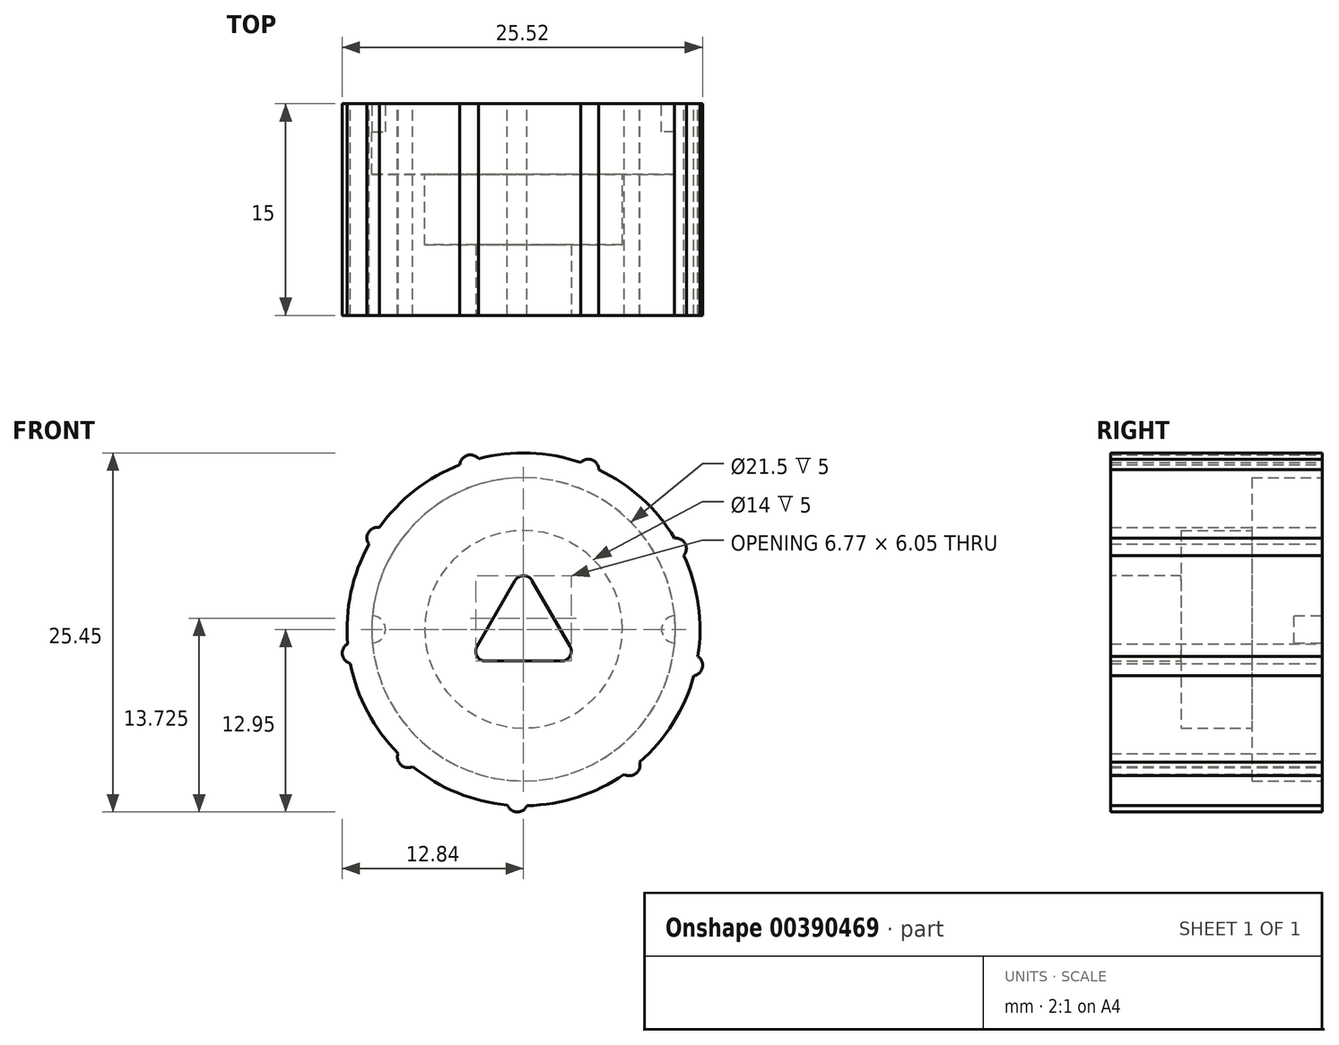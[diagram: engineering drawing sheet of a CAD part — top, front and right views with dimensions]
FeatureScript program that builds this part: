
annotation { "Feature Type Name" : "Feature", "Feature Type Description" : "" }
export const myFeature = defineFeature(function(context is Context, id is Id, definition is map)
    precondition{}
    {
        {
            var Q0;
            Q0=qCreatedBy(makeId("Front.planeOp"),FACE);
            var sketch = newSketch(context, id + "F0", { "sketchPlane" : qUnion([Q0])});
            skCircle(sketch, "E0", {"center": v(0, 0) * mm, "radius": 12.5 * mm});
            skCircle(sketch, "E1.cCircle", {"center": v(0, 0) * mm, "radius": 4.5 * mm, "construction": true});
            skLineSegment(sketch, "E1.0", {"start": v(0, 4.5) * mm, "end": v(3.9, -2.25) * mm});
            skLineSegment(sketch, "E1.1", {"start": v(3.9, -2.25) * mm, "end": v(-3.9, -2.25) * mm});
            skLineSegment(sketch, "E1.2", {"start": v(-3.9, -2.25) * mm, "end": v(0, 4.5) * mm});
            skSolve(sketch);
        }
        {
            var Q0;
            Q0=makeQuery(id+"F0.imprint","IMPRINT",FACE,{"disambiguationData":[TD([[makeQuery(id+"F0.imprint","IMPRINT",EDGE,{"derivedFrom":sQuery(id+"F0.wireOp",EDGE,"E0")}),1.0]])]});
            var Q1;
            Q1=sQuery(id+"F0.wireOp",EDGE,"E0");
            extrude(context, id + "F1", {"entities" : qUnion([Q0]), "surfaceEntities" : qUnion([Q1]), "depth" : 15 * mm});
        }
        {
            var Q0;
            Q0=makeQuery(id+"F1.opExtrude","CAP_FACE",FACE,{"disambiguationData":[OSD([sQuery(id+"F0.wireOp",EDGE,"E0"),sQuery(id+"F0.wireOp",EDGE,"E1.0"),sQuery(id+"F0.wireOp",EDGE,"E1.1"),sQuery(id+"F0.wireOp",EDGE,"E1.2")])],"isStart":true});
            var sketch = newSketch(context, id + "F2", { "sketchPlane" : qUnion([Q0])});
            skCircle(sketch, "E2", {"center": v(0, 0) * mm, "radius": 10.75 * mm});
            skSolve(sketch);
        }
        {
            var Q0;
            Q0=makeQuery(id+"F2.imprint","IMPRINT",FACE,{"disambiguationData":[TD([[makeQuery(id+"F2.imprint","IMPRINT",EDGE,{"derivedFrom":sQuery(id+"F2.wireOp",EDGE,"E2")}),1.0]])]});
            var Q1;
            Q1=sQuery(id+"F2.wireOp",EDGE,"E2");
            extrude(context, id + "F3", {"entities" : qUnion([Q0]), "operationType" : NewBodyOperationType.REMOVE, "surfaceEntities" : qUnion([Q1]), "oppositeDirection" : true, "depth" : 5 * mm});
        }
        {
            var Q0;
            Q0=makeQuery(id+"F3.boolean.opBoolean","COPY",FACE,{"derivedFrom":makeQuery(id+"F3.opExtrude","CAP_FACE",FACE,{"disambiguationData":[OSD([sQuery(id+"F0.wireOp",EDGE,"E1.0"),sQuery(id+"F0.wireOp",EDGE,"E1.1"),sQuery(id+"F0.wireOp",EDGE,"E1.2"),sQuery(id+"F2.wireOp",EDGE,"E2")])],"isStart":false})});
            var sketch = newSketch(context, id + "F4", { "sketchPlane" : qUnion([Q0])});
            skCircle(sketch, "E3", {"center": v(0, 0) * mm, "radius": 7 * mm});
            skSolve(sketch);
        }
        {
            var Q0;
            Q0 = qSketchRegion(id + "F4", true);
            extrude(context, id + "F5", {"entities" : qUnion([Q0]), "operationType" : NewBodyOperationType.REMOVE, "oppositeDirection" : true, "depth" : 5 * mm});
        }
        {
            var Q0;
            Q0=makeQuery(id+"F1.opExtrude","SWEPT_EDGE",EDGE,{"disambiguationData":[OSD([sQuery(id+"F0.wireOp",EDGE,"E1.0"),sQuery(id+"F0.wireOp",EDGE,"E1.2")])]});
            var Q1;
            Q1=makeQuery(id+"F1.opExtrude","SWEPT_EDGE",EDGE,{"disambiguationData":[OSD([sQuery(id+"F0.wireOp",EDGE,"E1.1"),sQuery(id+"F0.wireOp",EDGE,"E1.2")])]});
            var Q2;
            Q2=makeQuery(id+"F1.opExtrude","SWEPT_EDGE",EDGE,{"disambiguationData":[OSD([sQuery(id+"F0.wireOp",EDGE,"E1.0"),sQuery(id+"F0.wireOp",EDGE,"E1.1")])]});
            fillet(context, id + "F6", {"entities" : qUnion([Q0, Q1, Q2]), "radius" : 0.7 * mm, "tangentPropagation" : true, "allowEdgeOverflow" : false});
        }
        {
            var Q0;
            Q0=makeQuery(id+"F1.opExtrude","CAP_FACE",FACE,{"disambiguationData":[OSD([sQuery(id+"F0.wireOp",EDGE,"E0"),sQuery(id+"F0.wireOp",EDGE,"E1.0"),sQuery(id+"F0.wireOp",EDGE,"E1.1"),sQuery(id+"F0.wireOp",EDGE,"E1.2")])],"isStart":true});
            var sketch = newSketch(context, id + "F7", { "sketchPlane" : qUnion([Q0])});
            skCircle(sketch, "E4", {"center": v(-10.75, 0) * mm, "radius": 0.97 * mm});
            skCircle(sketch, "E5.1.0", {"center": v(10.75, 0) * mm, "radius": 0.97 * mm});
            skPoint(sketch, "E5.center", {"position": v(0, 0) * mm});
            skSolve(sketch);
        }
        {
            var Q0;
            {var subQ0=sQuery(id+"F7.wireOp",EDGE,"E4");var subQ1=makeQuery(id+"F3.boolean.opBoolean","COPY",EDGE,{"derivedFrom":makeQuery(id+"F3.opExtrude","CAP_EDGE",EDGE,{"disambiguationData":[OSD([sQuery(id+"F2.wireOp",EDGE,"E2")])],"isStart":true})});var subQ2=makeQuery(id+"F7.imprint","INTERSECT",VERTEX,{"disambiguationData":[OD(0.0)],"derivedFrom":[subQ1,subQ0]});Q0=makeQuery(id+"F7.imprint","IMPRINT",FACE,{"disambiguationData":[TD([[makeQuery(id+"F7.imprint","IMPRINT",EDGE,{"disambiguationData":[TD([[subQ2,-1.0]])],"derivedFrom":subQ0}),1.0]])]});}
            var Q1;
            {var subQ0=sQuery(id+"F7.wireOp",EDGE,"E5.1.0");var subQ1=makeQuery(id+"F3.boolean.opBoolean","COPY",EDGE,{"derivedFrom":makeQuery(id+"F3.opExtrude","CAP_EDGE",EDGE,{"disambiguationData":[OSD([sQuery(id+"F2.wireOp",EDGE,"E2")])],"isStart":true})});var subQ2=makeQuery(id+"F7.imprint","INTERSECT",VERTEX,{"disambiguationData":[OD(0.0)],"derivedFrom":[subQ1,subQ0]});Q1=makeQuery(id+"F7.imprint","IMPRINT",FACE,{"disambiguationData":[TD([[makeQuery(id+"F7.imprint","IMPRINT",EDGE,{"disambiguationData":[TD([[subQ2,1.0]])],"derivedFrom":subQ0}),1.0]])]});}
            extrude(context, id + "F8", {"entities" : qUnion([Q0, Q1]), "operationType" : NewBodyOperationType.ADD, "oppositeDirection" : true, "depth" : 2 * mm, "offsetDistance" : 25 * mm});
        }
        {
            var Q0;
            Q0=qCreatedBy(makeId("Front.planeOp"),FACE);
            var sketch = newSketch(context, id + "F9", { "sketchPlane" : qUnion([Q0])});
            skCircle(sketch, "E6", {"center": v(-10.34, 6.48) * mm, "radius": 0.75 * mm});
            skLineSegment(sketch, "E7", {"start": v(0, 14.1) * mm, "end": v(0, -18.46) * mm});
            skCircle(sketch, "E8.1.0", {"center": v(-12.09, -1.69) * mm, "radius": 0.75 * mm});
            skCircle(sketch, "E8.2.0", {"center": v(-8.18, -9.06) * mm, "radius": 0.75 * mm});
            skCircle(sketch, "E8.3.0", {"center": v(-0.44, -12.2) * mm, "radius": 0.75 * mm});
            skCircle(sketch, "E8.4.0", {"center": v(7.5, -9.62) * mm, "radius": 0.75 * mm});
            skCircle(sketch, "E8.5.0", {"center": v(11.93, -2.55) * mm, "radius": 0.75 * mm});
            skCircle(sketch, "E8.6.0", {"center": v(10.78, 5.72) * mm, "radius": 0.75 * mm});
            skCircle(sketch, "E8.7.0", {"center": v(4.58, 11.3) * mm, "radius": 0.75 * mm});
            skCircle(sketch, "E8.8.0", {"center": v(-3.76, 11.61) * mm, "radius": 0.75 * mm});
            skPoint(sketch, "E8.center", {"position": v(0, 0) * mm});
            skSolve(sketch);
        }
        {
            var Q0;
            Q0 = qSketchRegion(id + "F9", true);
            extrude(context, id + "F10", {"entities" : qUnion([Q0]), "operationType" : NewBodyOperationType.ADD, "depth" : 15 * mm});
        }
    });
